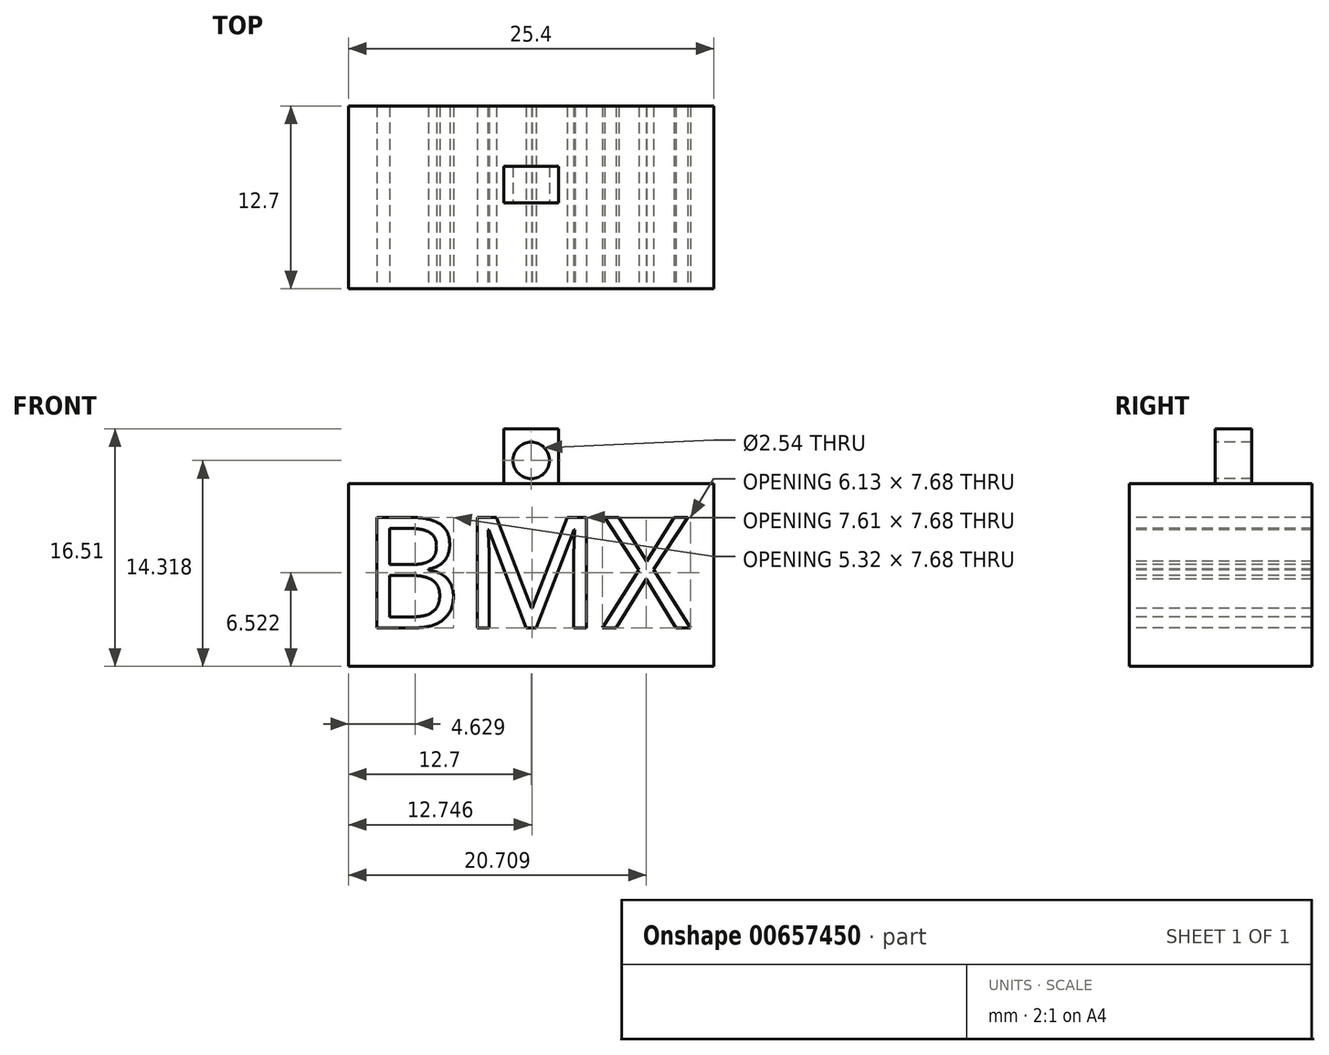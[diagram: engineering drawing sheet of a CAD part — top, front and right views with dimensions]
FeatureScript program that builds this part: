
annotation { "Feature Type Name" : "Feature", "Feature Type Description" : "" }
export const myFeature = defineFeature(function(context is Context, id is Id, definition is map)
    precondition{}
    {
        {
            var Q0;
            Q0=qCreatedBy(makeId("Front.planeOp"),FACE);
            var sketch = newSketch(context, id + "F0", { "sketchPlane" : qUnion([Q0])});
            skLineSegment(sketch, "E0.bottom", {"start": v(12.7, 6.35) * mm, "end": v(-12.7, 6.35) * mm});
            skLineSegment(sketch, "E0.top", {"start": v(12.7, -6.35) * mm, "end": v(-12.7, -6.35) * mm});
            skLineSegment(sketch, "E0.left", {"start": v(12.7, 6.35) * mm, "end": v(12.7, -6.35) * mm});
            skLineSegment(sketch, "E0.right", {"start": v(-12.7, 6.35) * mm, "end": v(-12.7, -6.35) * mm});
            skPoint(sketch, "E0.middle", {"position": v(0, 0) * mm});
            skSolve(sketch);
        }
        {
            var Q0;
            Q0=makeQuery(id+"F0.imprint","IMPRINT",FACE,{"disambiguationData":[TD([[makeQuery(id+"F0.imprint","IMPRINT",EDGE,{"derivedFrom":sQuery(id+"F0.wireOp",EDGE,"E0.bottom")}),1.0]])]});
            extrude(context, id + "F1", {"entities" : qUnion([Q0]), "depth" : 12.7 * mm, "offsetDistance" : 25.4 * mm});
        }
        {
            var Q0;
            Q0=makeQuery(id+"F1.opExtrude","CAP_FACE",FACE,{"disambiguationData":[OSD([sQuery(id+"F0.wireOp",EDGE,"E0.bottom"),sQuery(id+"F0.wireOp",EDGE,"E0.top"),sQuery(id+"F0.wireOp",EDGE,"E0.left"),sQuery(id+"F0.wireOp",EDGE,"E0.right")])],"isStart":false});
            var sketch = newSketch(context, id + "F2", { "sketchPlane" : qUnion([Q0])});
            skText(sketch, "E1", { "text": "BMX", "fontName": "OpenSans-Regular.ttf"});
            const initialGuessF2  = {"E1": [-0.01179, -0.00367, 1, 0, 0.00775]};
            skSetInitialGuess(sketch, initialGuessF2);
            skSolve(sketch);
        }
        {
            var Q0;
            Q0 = qSketchRegion(id + "F2", true);
            extrude(context, id + "F3", {"entities" : qUnion([Q0]), "operationType" : NewBodyOperationType.REMOVE, "oppositeDirection" : true, "depth" : 35.84 * mm, "offsetDistance" : 25.4 * mm});
        }
        {
            var Q0;
            Q0=makeQuery(id+"F1.opExtrude","SWEPT_FACE",FACE,{"disambiguationData":[OSD([sQuery(id+"F0.wireOp",EDGE,"E0.bottom")])]});
            var sketch = newSketch(context, id + "F4", { "sketchPlane" : qUnion([Q0])});
            skLineSegment(sketch, "E2.bottom", {"start": v(-1.9, -6.74) * mm, "end": v(1.9, -6.74) * mm});
            skLineSegment(sketch, "E2.top", {"start": v(-1.9, -4.2) * mm, "end": v(1.9, -4.2) * mm});
            skLineSegment(sketch, "E2.left", {"start": v(-1.9, -6.74) * mm, "end": v(-1.9, -4.2) * mm});
            skLineSegment(sketch, "E2.right", {"start": v(1.9, -6.74) * mm, "end": v(1.9, -4.2) * mm});
            skPoint(sketch, "E2.middle", {"position": v(0, -5.47) * mm});
            skSolve(sketch);
        }
        {
            var Q0;
            Q0=makeQuery(id+"F4.imprint","IMPRINT",FACE,{"disambiguationData":[TD([[makeQuery(id+"F4.imprint","IMPRINT",EDGE,{"derivedFrom":sQuery(id+"F4.wireOp",EDGE,"E2.bottom")}),1.0]])]});
            extrude(context, id + "F5", {"entities" : qUnion([Q0]), "operationType" : NewBodyOperationType.ADD, "depth" : 3.8 * mm, "offsetDistance" : 25.4 * mm});
        }
        {
            var Q0;
            Q0=makeQuery(id+"F5.opExtrude","SWEPT_FACE",FACE,{"disambiguationData":[OSD([sQuery(id+"F4.wireOp",EDGE,"E2.bottom")])]});
            var sketch = newSketch(context, id + "F6", { "sketchPlane" : qUnion([Q0])});
            skCircle(sketch, "E3", {"center": v(0, 7.97) * mm, "radius": 1.27 * mm});
            skSolve(sketch);
        }
        {
            var Q0;
            Q0=makeQuery(id+"F6.imprint","IMPRINT",FACE,{"disambiguationData":[TD([[makeQuery(id+"F6.imprint","IMPRINT",EDGE,{"derivedFrom":sQuery(id+"F6.wireOp",EDGE,"E3")}),1.0]])]});
            extrude(context, id + "F7", {"entities" : qUnion([Q0]), "operationType" : NewBodyOperationType.REMOVE, "oppositeDirection" : true, "depth" : 25.4 * mm, "offsetDistance" : 25.4 * mm});
        }
    });
